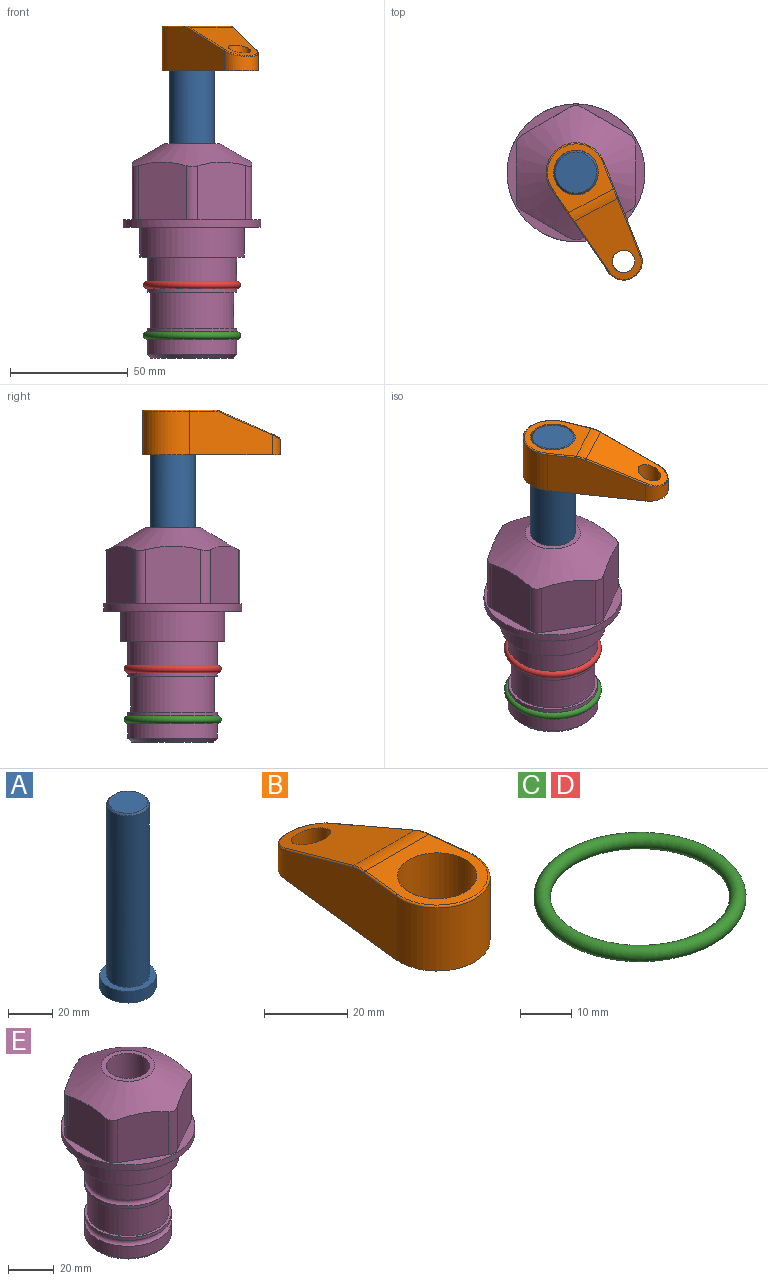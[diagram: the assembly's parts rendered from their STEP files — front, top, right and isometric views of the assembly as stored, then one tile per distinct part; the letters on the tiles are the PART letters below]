
ASSEMBLY  parts=5 mates=3
PART A: 6 faces, bbox 25.4x25.4x101.6 mm
  f0: plane 17.46x17.46mm, normal (0,0,1), area 239.5mm2, adj f5
  f1: plane 25.4x25.4mm, normal (0,0,-1), area 506.7mm2, adj f2
  f2: cylinder r=12.7mm len=25.4mm, axis (0,0,1), area 506.7mm2, adj f1,f3
  f3: plane 25.4x25.4mm, normal (0,0,1), area 221.7mm2, adj f2,f4
  f4: cylinder r=9.53mm len=94.46mm, axis (0,0,1), area 5653mm2, adj f3,f5
  f5: cone r=8.73mm half-angle=45deg, axis (0,0,-1), area 64.4mm2, adj f0,f4
PART B: 44 faces, bbox 27.5x64.5x19.1 mm
  f0: plane 2.3x0.95mm, normal (0,0,-1), area 1mm2, adj f25,f30,f34
  f1: plane 63.5x25.4mm, normal (0,0,-1), area 561.7mm2, adj f2,f3,f4,f5,f6,f7,f19,f20
  f2: cylinder r=12.7mm len=25.4mm, axis (0,0,-1), area 792.2mm2, adj f1,f3,f5,f13
  f3: plane 42.33x18.54mm, normal (0.99,0.11,0), area 647mm2, adj f1,f2,f4,f11,f12,f14
  f4: cylinder r=7.94mm len=15.78mm, axis (0,0,-1), area 158.6mm2, adj f1,f3,f5,f16
  f5: plane 42.33x18.54mm, normal (-0.99,0.11,0), area 647mm2, adj f1,f2,f4,f15,f17,f18
  f6: cylinder r=9.53mm len=19.05mm, axis (0,0,-1), area 1140.1mm2, adj f1,f8
  f7: cylinder r=4.76mm len=10.98mm, axis (0,0,-1), area 276.1mm2, adj f1,f9
  f8: plane 25.83x24.38mm, normal (0,0,1), area 262.2mm2, adj f6,f10,f11,f13,f15
  f9: plane 32.49x20.55mm, normal (0,0.34,0.94), area 489.9mm2, adj f7,f10,f14,f16,f18
  f10: cylinder r=12.7mm len=21.49mm, axis (-1,0,0), area 93.2mm2, adj f8,f9,f12,f17
  f11: cylinder r=0.51mm len=12.34mm, axis (0.11,-0.99,0), area 9.9mm2, adj f3,f8,f12,f13
  f12: bspline ~7.62x1.64mm, area 3.5mm2, adj f3,f10,f11,f14
  f13: torus R=12.19mm, axis (0,0,1), area 33.6mm2, adj f2,f8,f11,f15
  f14: cylinder r=0.51mm len=26.01mm, axis (0.1,-0.93,0.34), area 21.6mm2, adj f3,f9,f12,f16
  f15: cylinder r=0.51mm len=12.34mm, axis (0.11,0.99,0), area 9.9mm2, adj f5,f8,f13,f17
  f16: bspline ~15.78x7.05mm, area 15.7mm2, adj f4,f9,f14,f18
  f17: bspline ~7.62x1.64mm, area 3.5mm2, adj f5,f10,f15,f18
  f18: cylinder r=0.51mm len=26.01mm, axis (0.1,0.93,-0.34), area 21.6mm2, adj f5,f9,f16,f17
  f19: plane 21.6x14.29mm, normal (-0.99,-0.11,0), area 242.6mm2, adj f1,f26,f28,f34,f36,f38
  f20: plane 21.6x14.29mm, normal (0.99,-0.11,0), area 242.6mm2, adj f1,f27,f29,f37,f39,f41
  f21: cylinder r=12.7mm len=14.29mm, axis (0,0,-1), area 173.2mm2, adj f1,f26,f27,f30,f31,f33
  f22: cylinder r=7.94mm len=7.63mm, axis (0,0,-1), area 53.8mm2, adj f1,f28,f29,f42
  f23: plane 2.3x0.95mm, normal (0,0,-1), area 1mm2, adj f25,f33,f37
  f24: plane 17.94x12.32mm, normal (0,-0.34,-0.94), area 191.2mm2, adj f25,f38,f41,f42
  f25: cylinder r=9.53mm len=12.93mm, axis (-1,0,0), area 37.5mm2, adj f0,f23,f24,f31,f36,f39
  f26: cylinder r=1.59mm len=14.29mm, axis (0,0,-1), area 49mm2, adj f1,f19,f21,f32
  f27: cylinder r=1.59mm len=14.29mm, axis (0,0,-1), area 49mm2, adj f1,f20,f21,f35
  f28: cylinder r=1.59mm len=7.28mm, axis (0,0,-1), area 22.1mm2, adj f1,f19,f22,f40
  f29: cylinder r=1.59mm len=7.28mm, axis (0,0,-1), area 22.1mm2, adj f1,f20,f22,f43
  f30: torus R=14.29mm, axis (0,0,1), area 5.8mm2, adj f0,f21,f31,f32
  f31: bspline ~11.06x2.73mm, area 20.8mm2, adj f21,f25,f30,f33
  f32: sphere r=1.59mm, area 5.4mm2, adj f26,f30,f34
  f33: torus R=14.29mm, axis (0,0,1), area 5.8mm2, adj f21,f23,f31,f35
  f34: cylinder r=1.59mm len=1.68mm, axis (-0.11,0.99,0), area 2.4mm2, adj f0,f19,f32,f36
  f35: sphere r=1.59mm, area 5.4mm2, adj f27,f33,f37
  f36: bspline ~5.82x2.33mm, area 7.7mm2, adj f19,f25,f34,f38
  f37: cylinder r=1.59mm len=1.68mm, axis (0.11,0.99,0), area 2.4mm2, adj f20,f23,f35,f39
  f38: cylinder r=1.59mm len=18.33mm, axis (0.1,-0.93,0.34), area 46.7mm2, adj f19,f24,f36,f40
  f39: bspline ~5.82x2.33mm, area 7.7mm2, adj f20,f25,f37,f41
  f40: sphere r=1.59mm, area 3.6mm2, adj f28,f38,f42
  f41: cylinder r=1.59mm len=18.33mm, axis (0.1,0.93,-0.34), area 46.7mm2, adj f20,f24,f39,f43
  f42: bspline ~8.31x1.84mm, area 15.3mm2, adj f22,f24,f40,f43
  f43: sphere r=1.59mm, area 3.6mm2, adj f29,f41,f42
PART C: 1 faces, bbox 44.7x44.7x3.2 mm
  f0: torus R=19.05mm, axis (0,0,1), area 1193.9mm2
PART D: same geometry as C
PART E: 36 faces, bbox 58.7x58.7x91.2 mm
  f0: cylinder r=17.78mm len=35.56mm, axis (0,0,1), area 1670.8mm2, adj f23,f24,f31
  f1: cylinder r=19.05mm len=38.1mm, axis (0,0,1), area 1191.9mm2, adj f26,f27,f30
  f2: plane 58.66x58.66mm, normal (0,0,-1), area 1150.6mm2, adj f3,f28
  f3: cylinder r=29.33mm len=58.66mm, axis (0,0,-1), area 585.1mm2, adj f2,f4
  f4: plane 58.66x58.66mm, normal (0,0,1), area 475.9mm2, adj f3,f5,f6,f7,f8,f9,f10,f11
  f5: plane 24.5x20.32mm, normal (-0.5,0.87,0), area 562.8mm2, adj f4,f15,f16,f17
  f6: plane 24.5x20.32mm, normal (0.5,0.87,0), area 562.8mm2, adj f4,f14,f15,f17
  f7: plane 24.5x23.48mm, normal (1,0,0), area 562.8mm2, adj f4,f13,f14,f17
  f8: plane 24.5x20.32mm, normal (0.5,-0.87,0), area 562.8mm2, adj f4,f12,f13,f17
  f9: plane 24.5x20.32mm, normal (-0.5,-0.87,0), area 562.8mm2, adj f4,f11,f12,f17
  f10: plane 24.5x23.48mm, normal (-1,0,0), area 562.8mm2, adj f4,f11,f16,f17
  f11: cylinder r=5.08mm len=23.01mm, axis (0,0,-1), area 121.2mm2, adj f4,f9,f10,f17
  f12: cylinder r=5.08mm len=23.01mm, axis (0,0,-1), area 121.2mm2, adj f4,f8,f9,f17
  f13: cylinder r=5.08mm len=23.01mm, axis (0,0,-1), area 121.2mm2, adj f4,f7,f8,f17
  f14: cylinder r=5.08mm len=23.01mm, axis (0,0,-1), area 121.2mm2, adj f4,f6,f7,f17
  f15: cylinder r=5.08mm len=23.01mm, axis (0,0,-1), area 121.2mm2, adj f4,f5,f6,f17
  f16: cylinder r=5.08mm len=23.01mm, axis (0,0,-1), area 121.2mm2, adj f4,f5,f10,f17
  f17: cone r=11.73mm half-angle=60deg, axis (0,0,-1), area 2071.8mm2, adj f5,f6,f7,f8,f9,f10,f11,f12
  f18: plane 23.46x23.46mm, normal (0,0,1), area 147.4mm2, adj f17,f35
  f19: plane 34.93x34.93mm, normal (0,0,-1), area 958mm2, adj f29
  f20: cylinder r=19.05mm len=38.1mm, axis (0,0,1), area 760.1mm2, adj f21,f29
  f21: torus R=19.05mm, axis (0,0,1), area 565.3mm2, adj f20,f22
  f22: cylinder r=19.05mm len=38.1mm, axis (0,0,1), area 190mm2, adj f21,f23
  f23: plane 38.1x38.1mm, normal (0,0,1), area 146.9mm2, adj f0,f22
  f24: plane 38.1x38.1mm, normal (0,0,-1), area 146.9mm2, adj f0,f25
  f25: cylinder r=19.05mm len=38.1mm, axis (0,0,1), area 190mm2, adj f24,f26
  f26: torus R=19.05mm, axis (0,0,1), area 565.3mm2, adj f1,f25
  f27: plane 44.45x44.45mm, normal (0,0,-1), area 411.7mm2, adj f1,f28
  f28: cylinder r=22.23mm len=44.45mm, axis (0,0,1), area 1773.5mm2, adj f2,f27
  f29: cone r=19.05mm half-angle=45deg, axis (0,0,1), area 257.5mm2, adj f19,f20
  f30: cylinder r=3.17mm len=6.75mm, axis (-1,0,0), area 128mm2, adj f1,f33
  f31: cylinder r=3.17mm len=6.35mm, axis (-1,0,0), area 102.5mm2, adj f0,f33
  f32: plane 25.4x25.4mm, normal (0,0,1), area 506.7mm2, adj f33
  f33: cylinder r=12.7mm len=66.42mm, axis (0,0,-1), area 5236.2mm2, adj f30,f31,f32,f34
  f34: cone r=9.53mm half-angle=30deg, axis (0,0,-1), area 443.4mm2, adj f33,f35
  f35: cylinder r=9.53mm len=19.05mm, axis (0,0,-1), area 849mm2, adj f18,f34
PLACE A rot(axis=(0,0,-1),61.8deg) t=(0,0,11.91)mm
PLACE B rot(axis=(0,0,-1),151.8deg) t=(0,0,66.52)mm
PLACE C t=(0,0,-21.59)mm
PLACE D at identity
PLACE E at identity fixed
MATE fastened C.f0 <-> E.f0  axis (0,0,1) through (0,0,-46.1)mm
MATE cylindrical A.f2 <-> E.f0  axis (0,0,1) through (0,0,37.55)mm
MATE fastened B.f2 <-> A.f2  axis (0,0,1) through (0,0,85.57)mm
